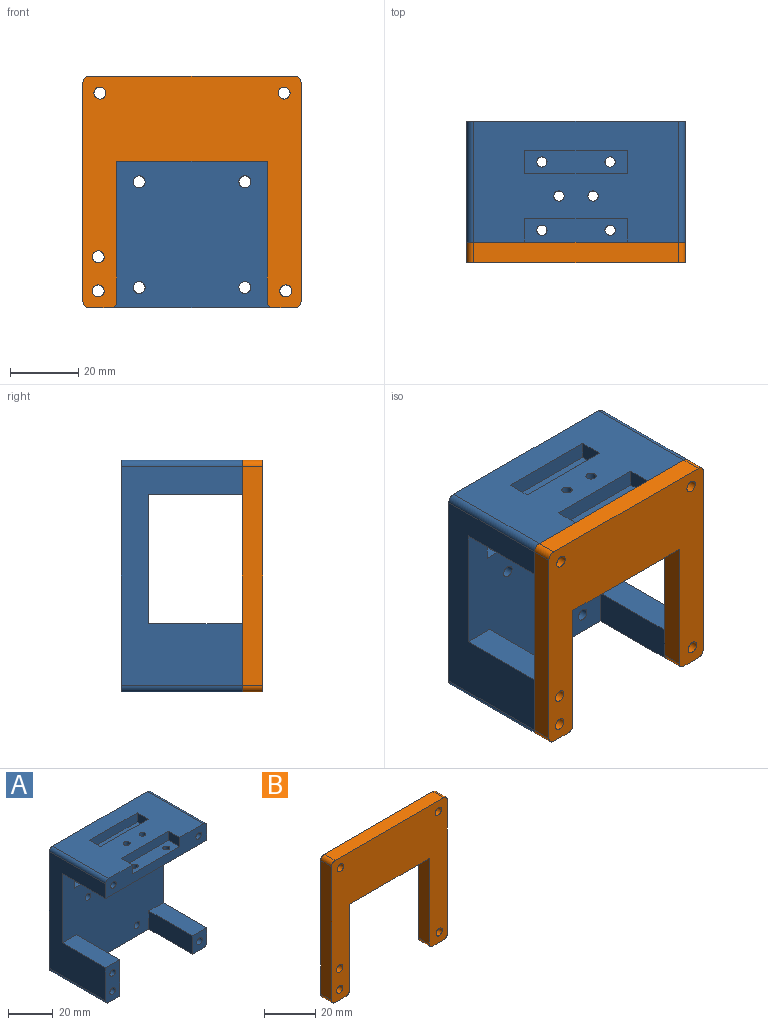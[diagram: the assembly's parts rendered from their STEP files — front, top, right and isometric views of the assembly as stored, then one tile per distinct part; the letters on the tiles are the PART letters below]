
ASSEMBLY  parts=2 mates=1
PART A: 60 faces, bbox 64x35.5x68 mm
  f0: plane 68x64mm, normal (0,1,0), area 4182mm2, adj f5,f11,f12,f13,f14,f15,f18,f19
  f1: plane 64x58mm, normal (0,-1,0), area 3323.5mm2, adj f2,f11,f12,f13,f16,f17,f21,f22
  f2: plane 64x27.5mm, normal (0,0,-1), area 1659.7mm2, adj f1,f6,f7,f8,f9,f10,f11,f13
  f3: cylinder r=1.5mm len=7mm, axis (0,0,1), area 66mm2, adj f5,f39
  f4: cylinder r=1.5mm len=7mm, axis (0,0,1), area 66mm2, adj f5,f34
  f5: plane 60x35.5mm, normal (0,0,1), area 1695.9mm2, adj f0,f3,f4,f6,f26,f27,f28,f29
  f6: plane 64x10mm, normal (0,-1,0), area 469mm2, adj f2,f5,f11,f13,f14,f15,f30,f31
  f7: cylinder r=1.5mm len=5mm, axis (0,0,1), area 47.1mm2, adj f2,f25
  f8: cylinder r=1.5mm len=5mm, axis (0,0,1), area 47.1mm2, adj f2,f30
  f9: cylinder r=1.5mm len=5mm, axis (0,0,1), area 47.1mm2, adj f2,f30
  f10: cylinder r=1.5mm len=5mm, axis (0,0,1), area 47.1mm2, adj f2,f25
  f11: plane 64x35.5mm, normal (-1,0,0), area 1227mm2, adj f0,f1,f2,f6,f17,f20,f56,f57
  f12: plane 60x35.5mm, normal (0,0,-1), area 865mm2, adj f0,f1,f16,f20,f22,f24,f57,f58
  f13: plane 64x35.5mm, normal (1,0,0), area 952mm2, adj f0,f1,f2,f6,f21,f24,f58,f59
  f14: cylinder r=1.75mm len=35.5mm, axis (0,1,0), area 390.3mm2, adj f0,f6
  f15: cylinder r=1.75mm len=35.5mm, axis (0,1,0), area 390.3mm2, adj f0,f6
  f16: plane 27.5x20mm, normal (1,0,0), area 550mm2, adj f1,f12,f17,f20
  f17: plane 27.5x9mm, normal (0,0,1), area 247.5mm2, adj f1,f11,f16,f20
  f18: cylinder r=1.75mm len=35.5mm, axis (0,1,0), area 390.3mm2, adj f0,f20
  f19: cylinder r=1.75mm len=35.5mm, axis (0,1,0), area 390.3mm2, adj f0,f20
  f20: plane 20x9mm, normal (0,-1,0), area 159.9mm2, adj f11,f12,f16,f17,f18,f19,f57
  f21: plane 27.5x9mm, normal (0,0,1), area 247.5mm2, adj f1,f13,f22,f24
  f22: plane 27.5x10mm, normal (-1,0,0), area 275mm2, adj f1,f12,f21,f24
  f23: cylinder r=1.75mm len=35.5mm, axis (0,1,0), area 390.3mm2, adj f0,f24
  f24: plane 10x9mm, normal (0,-1,0), area 79.5mm2, adj f12,f13,f21,f22,f23,f58
  f25: plane 30x7mm, normal (0,0,1), area 195.9mm2, adj f7,f10,f26,f27,f28,f29
  f26: plane 7x5mm, normal (1,0,0), area 35mm2, adj f5,f25,f27,f29
  f27: plane 30x5mm, normal (0,1,0), area 150mm2, adj f5,f25,f26,f28
  f28: plane 7x5mm, normal (-1,0,0), area 35mm2, adj f5,f25,f27,f29
  f29: plane 30x5mm, normal (0,-1,0), area 150mm2, adj f5,f25,f26,f28
  f30: plane 30x7mm, normal (0,0,1), area 195.9mm2, adj f6,f8,f9,f31,f32,f33
  f31: plane 7x5mm, normal (-1,0,0), area 35mm2, adj f5,f6,f30,f32
  f32: plane 30x5mm, normal (0,-1,0), area 150mm2, adj f5,f30,f31,f33
  f33: plane 7x5mm, normal (1,0,0), area 35mm2, adj f5,f6,f30,f32
  f34: plane 6x6mm, normal (0,0,-1), area 28.9mm2, adj f4,f35,f36,f37,f38
  f35: plane 6x3mm, normal (1,0,0), area 18mm2, adj f2,f34,f36,f38
  f36: plane 6x3mm, normal (0,-1,0), area 18mm2, adj f2,f34,f35,f37
  f37: plane 6x3mm, normal (-1,0,0), area 18mm2, adj f2,f34,f36,f38
  f38: plane 6x3mm, normal (0,1,0), area 18mm2, adj f2,f34,f35,f37
  f39: plane 6x6mm, normal (0,0,-1), area 28.9mm2, adj f3,f40,f41,f42,f43
  f40: plane 6x3mm, normal (0,-1,0), area 18mm2, adj f2,f39,f41,f43
  f41: plane 6x3mm, normal (-1,0,0), area 18mm2, adj f2,f39,f40,f42
  f42: plane 6x3mm, normal (0,1,0), area 18mm2, adj f2,f39,f41,f43
  f43: plane 6x3mm, normal (1,0,0), area 18mm2, adj f2,f39,f40,f42
  f44: cylinder r=1.75mm len=8mm, axis (0,-1,0), area 88mm2, adj f0,f1
  f45: cylinder r=1.75mm len=8mm, axis (0,-1,0), area 88mm2, adj f0,f1
  f46: cylinder r=1.75mm len=8mm, axis (0,-1,0), area 88mm2, adj f0,f1
  f47: cylinder r=1.75mm len=8mm, axis (0,-1,0), area 88mm2, adj f0,f1
  f48: plane 10x8mm, normal (-1,0,0), area 80mm2, adj f0,f1,f49,f51
  f49: plane 8x4mm, normal (0,0,-1), area 32mm2, adj f0,f1,f48,f50
  f50: plane 10x8mm, normal (1,0,0), area 80mm2, adj f0,f1,f49,f51
  f51: plane 8x4mm, normal (0,0,1), area 32mm2, adj f0,f1,f48,f50
  f52: plane 8x4mm, normal (0,0,-1), area 32mm2, adj f0,f1,f53,f55
  f53: plane 10x8mm, normal (1,0,0), area 80mm2, adj f0,f1,f52,f54
  f54: plane 8x4mm, normal (0,0,1), area 32mm2, adj f0,f1,f53,f55
  f55: plane 10x8mm, normal (-1,0,0), area 80mm2, adj f0,f1,f52,f54
  f56: cylinder r=2mm len=35.5mm, axis (0,-1,0), area 111.5mm2, adj f0,f5,f6,f11
  f57: cylinder r=2mm len=35.5mm, axis (0,1,0), area 111.5mm2, adj f0,f11,f12,f20
  f58: cylinder r=2mm len=35.5mm, axis (0,-1,0), area 111.5mm2, adj f0,f12,f13,f24
  f59: cylinder r=2mm len=35.5mm, axis (0,1,0), area 111.5mm2, adj f0,f5,f6,f13
PART B: 21 faces, bbox 64x6x68 mm
  f0: plane 6x6mm, normal (0,0,-1), area 36mm2, adj f5,f6,f15,f19
  f1: plane 60x6mm, normal (0,0,1), area 360mm2, adj f5,f6,f17,f20
  f2: plane 64x6mm, normal (-1,0,0), area 384mm2, adj f5,f6,f17,f18
  f3: plane 6x6mm, normal (0,0,-1), area 36mm2, adj f5,f6,f16,f18
  f4: plane 64x6mm, normal (1,0,0), area 384mm2, adj f5,f6,f19,f20
  f5: plane 68x64mm, normal (0,-1,0), area 2406.7mm2, adj f0,f1,f2,f3,f4,f7,f8,f9
  f6: plane 68x64mm, normal (0,1,0), area 2406.7mm2, adj f0,f1,f2,f3,f4,f7,f8,f9
  f7: cylinder r=1.75mm len=6mm, axis (0,-1,0), area 66mm2, adj f5,f6
  f8: cylinder r=1.75mm len=6mm, axis (0,-1,0), area 66mm2, adj f5,f6
  f9: plane 44x6mm, normal (0,0,-1), area 264mm2, adj f5,f6,f10,f11
  f10: plane 41x6mm, normal (1,0,0), area 246mm2, adj f5,f6,f9,f16
  f11: plane 41x6mm, normal (-1,0,0), area 246mm2, adj f5,f6,f9,f15
  f12: cylinder r=1.75mm len=6mm, axis (0,-1,0), area 66mm2, adj f5,f6
  f13: cylinder r=1.75mm len=6mm, axis (0,-1,0), area 66mm2, adj f5,f6
  f14: cylinder r=1.75mm len=6mm, axis (0,-1,0), area 66mm2, adj f5,f6
  f15: cylinder r=2mm len=6mm, axis (0,1,0), area 18.8mm2, adj f0,f5,f6,f11
  f16: cylinder r=2mm len=6mm, axis (0,-1,0), area 18.8mm2, adj f3,f5,f6,f10
  f17: cylinder r=2mm len=6mm, axis (0,-1,0), area 18.8mm2, adj f1,f2,f5,f6
  f18: cylinder r=2mm len=6mm, axis (0,1,0), area 18.8mm2, adj f2,f3,f5,f6
  f19: cylinder r=2mm len=6mm, axis (0,-1,0), area 18.8mm2, adj f0,f4,f5,f6
  f20: cylinder r=2mm len=6mm, axis (0,1,0), area 18.8mm2, adj f1,f4,f5,f6
PLACE A t=(0,35.5,0)mm
PLACE B at identity
MATE fastened A.f56 <-> B.f17  axis (0,-1,0) through (-30,0,32)mm
